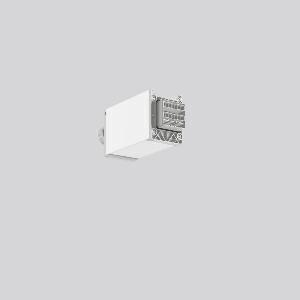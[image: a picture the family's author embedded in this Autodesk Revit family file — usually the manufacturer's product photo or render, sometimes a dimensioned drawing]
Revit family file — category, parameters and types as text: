
# Revit family: linedo_anfangseinspeisung_982859_002_1_2fe3
name_source: partatom
category: Lighting Fixtures
units: mm (PartAtom-declared; Revit-internal decimal feet)

## family parameters
Cut with Voids When Loaded = No
Host = Face
Light Source = No
Part Type = Normal
Room Calculation Point = No
Round Connector Dimension = Use Diameter
Shared = No

## types (1)
- LINEDO Anfangseinspeisung
    Apparent Load = 0 VA
    Default Elevation = 1800 mm
    Description = Series: LINEDO
Initial power feed (short Version), 7-pole, connection plug. Housing: extruded aluminium profile, powder-coated. Cover made of plastic, surface like housing. LINEDO plug system, plastic, light grey. 1 cable gland (M25). Cable gland on side or on top. Convenient connection with flat connector.
Colour: white
Length: 152 mm
Width: 58 mm
Height: 76 mm
Weight: 283 g
    Height = 76 mm
    Lamp = 0 x
    Length = 152 mm
    Luminous efficacy = 0 lm/W
    Manufacturer = RZB
    ModVariant = No
    Model = 982859.002.1
    Mounting Place = Ceiling
    Mounting Type = Surface mounted
    Number of Poles = 1
    OnlyDefault = Yes
    Power Factor = 1
    Product Name = LINEDO Anfangseinspeisung
    Product group = Surface mounted continuous line luminaire system
    ProductGroupID = 310
    Protection Class = Protection class I
    Protection Degree = Degree of protection
    RLX_Detail_Level = 1
    RLX_Emergency_Light_Flux = 0 lm
    RLX_Emergency_Type = 0
    RLX_Emergency_Type_DB = No
    RlxData = <blob elided: 13061 chars, md5=70562539>
    Standby Power = 0 W
    System Light Flux = 0 lm
    System Power = 0 W
    Type Comments = Product without accessories
    Type Image = 982859.002.1.jpg
    URL = http://relux.com
    VarID = ---
    Voltage = 0 V
    Weight = 0.00 kg
    Width = 58 mm

## geometry (parser evidence)
native form markers: Sweep x9
no freeform markers — native parametric forms only
